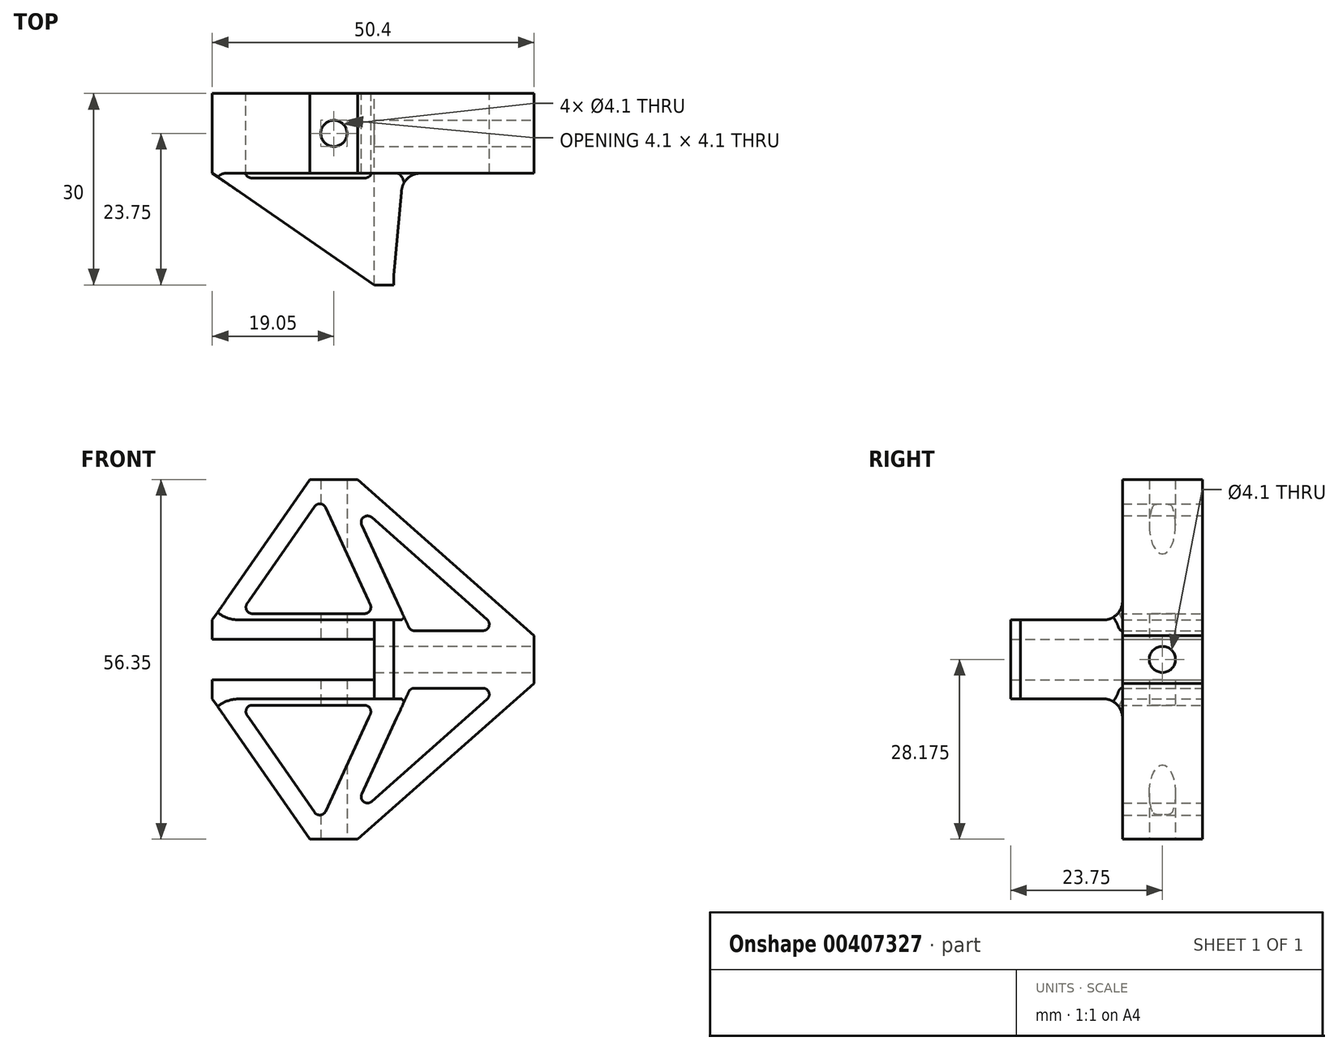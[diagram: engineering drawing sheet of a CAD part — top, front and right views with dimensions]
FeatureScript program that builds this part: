
annotation { "Feature Type Name" : "Feature", "Feature Type Description" : "" }
export const myFeature = defineFeature(function(context is Context, id is Id, definition is map)
    precondition{}
    {
        {
            var Q0;
            Q0=qCreatedBy(makeId("Front.planeOp"),FACE);
            var sketch = newSketch(context, id + "F0", { "sketchPlane" : qUnion([Q0])});
            skLineSegment(sketch, "E0", {"start": v(-37.84, 0) * mm, "end": v(0, 0) * mm, "construction": true});
            skLineSegment(sketch, "E1", {"start": v(0, 0) * mm, "end": v(0, -6.35) * mm, "construction": true});
            skLineSegment(sketch, "E2", {"start": v(0, -6.35) * mm, "end": v(-37.84, -6.35) * mm, "construction": true});
            skLineSegment(sketch, "E3", {"start": v(-12.7, -6.35) * mm, "end": v(-12.7, 0) * mm, "construction": true});
            skLineSegment(sketch, "E4", {"start": v(-4.3, -31.35) * mm, "end": v(-4.3, 20.4) * mm, "construction": true});
            skLineSegment(sketch, "E5", {"start": v(-4.3, 20.4) * mm, "end": v(-8.4, 20.4) * mm, "construction": true});
            skLineSegment(sketch, "E6", {"start": v(-8.4, 20.4) * mm, "end": v(-8.4, -31.35) * mm, "construction": true});
            skLineSegment(sketch, "E7", {"start": v(-8.4, -31.35) * mm, "end": v(-4.3, -31.35) * mm, "construction": true});
            skLineSegment(sketch, "E8", {"start": v(-6.35, -31.35) * mm, "end": v(-6.35, 20.4) * mm, "construction": true});
            skLineSegment(sketch, "E9", {"start": v(-25.4, -6.35) * mm, "end": v(-25.4, -9.35) * mm});
            skLineSegment(sketch, "E10", {"start": v(-25.4, -9.35) * mm, "end": v(-10.1, -31.35) * mm});
            skLineSegment(sketch, "E11", {"start": v(-10.1, -31.35) * mm, "end": v(-2.6, -31.35) * mm});
            skLineSegment(sketch, "E12", {"start": v(-2.6, -31.35) * mm, "end": v(25, -6.93) * mm});
            skLineSegment(sketch, "E13", {"start": v(25, -6.93) * mm, "end": v(25, -3.18) * mm});
            skLineSegment(sketch, "E14", {"start": v(0, -3.17) * mm, "end": v(-29.82, -3.17) * mm, "construction": true});
            skLineSegment(sketch, "E15", {"start": v(-25.4, -6.35) * mm, "end": v(0, -6.35) * mm});
            skLineSegment(sketch, "E16", {"start": v(0, -6.35) * mm, "end": v(0, -3.17) * mm});
            skLineSegment(sketch, "E17.MirrorCS", {"start": v(0, 0) * mm, "end": v(0, -3.17) * mm});
            skLineSegment(sketch, "E18.MirrorCS", {"start": v(-25.4, 0) * mm, "end": v(0, 0) * mm});
            skLineSegment(sketch, "E19.MirrorCS", {"start": v(-25.4, 0) * mm, "end": v(-25.4, 3) * mm});
            skLineSegment(sketch, "E20.MirrorCS", {"start": v(-25.4, 3) * mm, "end": v(-10.1, 25) * mm});
            skLineSegment(sketch, "E21.MirrorCS", {"start": v(-10.1, 25) * mm, "end": v(-2.6, 25) * mm});
            skLineSegment(sketch, "E22.MirrorCS", {"start": v(-2.6, 25) * mm, "end": v(25, 0.57) * mm});
            skLineSegment(sketch, "E23.MirrorCS", {"start": v(25, 0.57) * mm, "end": v(25, -3.18) * mm});
            skLineSegment(sketch, "E24", {"start": v(-19.96, -11.92) * mm, "end": v(-9.38, -27.13) * mm});
            skLineSegment(sketch, "E25", {"start": v(-7.65, -26.98) * mm, "end": v(-0.65, -11.77) * mm});
            skLineSegment(sketch, "E26", {"start": v(-1.56, -10.35) * mm, "end": v(-19.14, -10.35) * mm});
            skLineSegment(sketch, "E27", {"start": v(0, -3.17) * mm, "end": v(0, -28.47) * mm, "construction": true});
            skLineSegment(sketch, "E28", {"start": v(-0.42, -25.42) * mm, "end": v(17.65, -9.42) * mm});
            skLineSegment(sketch, "E29", {"start": v(16.99, -7.68) * mm, "end": v(6.27, -7.68) * mm});
            skLineSegment(sketch, "E30", {"start": v(5.37, -8.26) * mm, "end": v(-2, -24.25) * mm});
            skLineSegment(sketch, "E31", {"start": v(25, -5.22) * mm, "end": v(-10.9, -5.23) * mm, "construction": true});
            skLineSegment(sketch, "E32.MirrorCS", {"start": v(25, -1.13) * mm, "end": v(-10.9, -1.12) * mm, "construction": true});
            skLineSegment(sketch, "E33", {"start": v(-8.38, -28.56) * mm, "end": v(-3.98, -28.56) * mm, "construction": true});
            skPoint(sketch, "E34.visualSharp", {"position": v(-8.38, -28.56) * mm});
            skArc(sketch, "E34.filletArc", {"start": v(-9.38, -27.13) * mm, "mid": v(-8.47, -27.55) * mm, "end": v(-7.65, -26.98) * mm});
            skPoint(sketch, "E35.visualSharp", {"position": v(-3.98, -28.56) * mm});
            skArc(sketch, "E35.filletArc", {"start": v(-2, -24.25) * mm, "mid": v(-1.68, -25.47) * mm, "end": v(-0.42, -25.42) * mm});
            skPoint(sketch, "E36.visualSharp", {"position": v(19.63, -7.67) * mm});
            skArc(sketch, "E36.filletArc", {"start": v(17.65, -9.42) * mm, "mid": v(17.92, -8.32) * mm, "end": v(16.99, -7.68) * mm});
            skPoint(sketch, "E37.visualSharp", {"position": v(5.63, -7.67) * mm});
            skArc(sketch, "E37.filletArc", {"start": v(6.27, -7.67) * mm, "mid": v(5.74, -7.83) * mm, "end": v(5.37, -8.26) * mm});
            skPoint(sketch, "E38.visualSharp", {"position": v(0, -10.35) * mm});
            skArc(sketch, "E38.filletArc", {"start": v(-0.65, -11.77) * mm, "mid": v(-0.72, -10.81) * mm, "end": v(-1.56, -10.35) * mm});
            skPoint(sketch, "E39.visualSharp", {"position": v(-21.05, -10.35) * mm});
            skArc(sketch, "E39.filletArc", {"start": v(-19.14, -10.35) * mm, "mid": v(-20.02, -10.89) * mm, "end": v(-19.96, -11.92) * mm});
            skLineSegment(sketch, "E40.MirrorCS", {"start": v(-1.56, 4) * mm, "end": v(-19.14, 4) * mm});
            skArc(sketch, "E41.MirrorCS", {"start": v(-19.14, 4) * mm, "mid": v(-20.02, 4.54) * mm, "end": v(-19.96, 5.57) * mm});
            skLineSegment(sketch, "E42.MirrorCS", {"start": v(-19.96, 5.57) * mm, "end": v(-9.38, 20.78) * mm});
            skArc(sketch, "E43.MirrorCS", {"start": v(-9.38, 20.78) * mm, "mid": v(-8.47, 21.2) * mm, "end": v(-7.65, 20.63) * mm});
            skLineSegment(sketch, "E44.MirrorCS", {"start": v(-7.65, 20.63) * mm, "end": v(-0.65, 5.42) * mm});
            skArc(sketch, "E45.MirrorCS", {"start": v(-0.65, 5.42) * mm, "mid": v(-0.72, 4.46) * mm, "end": v(-1.56, 4) * mm});
            skLineSegment(sketch, "E46.MirrorCS", {"start": v(5.37, 1.9) * mm, "end": v(-2, 17.9) * mm});
            skArc(sketch, "E47.MirrorCS", {"start": v(-2, 17.9) * mm, "mid": v(-1.68, 19.12) * mm, "end": v(-0.42, 19.07) * mm});
            skLineSegment(sketch, "E48.MirrorCS", {"start": v(-0.42, 19.07) * mm, "end": v(17.65, 3.07) * mm});
            skArc(sketch, "E49.MirrorCS", {"start": v(17.65, 3.07) * mm, "mid": v(17.92, 1.97) * mm, "end": v(16.99, 1.33) * mm});
            skLineSegment(sketch, "E50.MirrorCS", {"start": v(16.99, 1.32) * mm, "end": v(6.27, 1.33) * mm});
            skArc(sketch, "E51.MirrorCS", {"start": v(6.27, 1.33) * mm, "mid": v(5.74, 1.48) * mm, "end": v(5.37, 1.9) * mm});
            skLineSegment(sketch, "E52", {"start": v(-25.4, -9.35) * mm, "end": v(3, -9.35) * mm});
            skLineSegment(sketch, "E53", {"start": v(-25.4, 3) * mm, "end": v(3, 3) * mm});
            skLineSegment(sketch, "E54", {"start": v(3, -9.35) * mm, "end": v(3, 3) * mm});
            skSolve(sketch);
        }
        {
            var Q0;
            Q0=makeQuery(id+"F0.imprint","IMPRINT",FACE,{"disambiguationData":[TD([[makeQuery(id+"F0.imprint","IMPRINT",EDGE,{"derivedFrom":sQuery(id+"F0.wireOp",EDGE,"E10")}),1.0]])]});
            var Q1;
            Q1=makeQuery(id+"F0.imprint","IMPRINT",FACE,{"disambiguationData":[TD([[makeQuery(id+"F0.imprint","IMPRINT",EDGE,{"derivedFrom":sQuery(id+"F0.wireOp",EDGE,"E9")}),1.0]])]});
            extrude(context, id + "F1", {"entities" : qUnion([Q0, Q1]), "depth" : 12.5 * mm});
        }
        {
            var Q0;
            Q0=makeQuery(id+"F0.imprint","IMPRINT",FACE,{"disambiguationData":[TD([[makeQuery(id+"F0.imprint","IMPRINT",EDGE,{"derivedFrom":sQuery(id+"F0.wireOp",EDGE,"E9")}),1.0]])]});
            extrude(context, id + "F2", {"entities" : qUnion([Q0]), "operationType" : NewBodyOperationType.ADD, "depth" : 30 * mm});
        }
        {
            var Q0;
            Q0=makeQuery(id+"F2.opExtrude","SWEPT_FACE",FACE,{"disambiguationData":[OSD([sQuery(id+"F0.wireOp",EDGE,"E53")])]});
            var sketch = newSketch(context, id + "F3", { "sketchPlane" : qUnion([Q0])});
            skLineSegment(sketch, "E55.1", {"start": v(3, -30) * mm, "end": v(3, -12.5) * mm});
            skLineSegment(sketch, "E55.2", {"start": v(3, -12.5) * mm, "end": v(-25.4, -12.5) * mm});
            skLineSegment(sketch, "E55.3", {"start": v(-25.4, -30) * mm, "end": v(-25.4, -12.5) * mm});
            skLineSegment(sketch, "E56.0", {"start": v(-25.4, -30) * mm, "end": v(0, -30) * mm});
            skLineSegment(sketch, "E57", {"start": v(0, -30) * mm, "end": v(-25.4, -12.5) * mm});
            skSolve(sketch);
        }
        {
            var Q0;
            Q0=makeQuery(id+"F3.imprint","IMPRINT",FACE,{"disambiguationData":[TD([[makeQuery(id+"F3.imprint","IMPRINT",EDGE,{"derivedFrom":sQuery(id+"F3.wireOp",EDGE,"E55.3")}),-1.0]])]});
            extrude(context, id + "F4", {"entities" : qUnion([Q0]), "operationType" : NewBodyOperationType.REMOVE, "endBound" : BoundingType.THROUGH_ALL, "oppositeDirection" : true, "depth" : 25 * mm});
        }
        {
            var Q0;
            Q0=makeQuery(id+"F1.opExtrude","SWEPT_FACE",FACE,{"disambiguationData":[OSD([sQuery(id+"F0.wireOp",EDGE,"E11")])]});
            var sketch = newSketch(context, id + "F5", { "sketchPlane" : qUnion([Q0])});
            skLineSegment(sketch, "E58", {"start": v(-6.35, 12.5) * mm, "end": v(-6.35, 0) * mm, "construction": true});
            skCircle(sketch, "E59", {"center": v(-6.35, 6.25) * mm, "radius": 2.05 * mm});
            skSolve(sketch);
        }
        {
            var Q0;
            Q0=makeQuery(id+"F5.imprint","IMPRINT",FACE,{"disambiguationData":[TD([[makeQuery(id+"F5.imprint","IMPRINT",EDGE,{"derivedFrom":sQuery(id+"F5.wireOp",EDGE,"E59")}),1.0]])]});
            extrude(context, id + "F6", {"entities" : qUnion([Q0]), "operationType" : NewBodyOperationType.REMOVE, "endBound" : BoundingType.THROUGH_ALL, "oppositeDirection" : true, "depth" : 25 * mm});
        }
        {
            var Q0;
            Q0=makeQuery(id+"F1.opExtrude","SWEPT_FACE",FACE,{"disambiguationData":[OSD([sQuery(id+"F0.wireOp",EDGE,"E13"),sQuery(id+"F0.wireOp",EDGE,"E23.MirrorCS")])]});
            var sketch = newSketch(context, id + "F7", { "sketchPlane" : qUnion([Q0])});
            skLineSegment(sketch, "E60", {"start": v(-12.5, -3.18) * mm, "end": v(0, -3.18) * mm, "construction": true});
            skCircle(sketch, "E61", {"center": v(-6.25, -3.18) * mm, "radius": 2.05 * mm});
            skSolve(sketch);
        }
        {
            var Q0;
            Q0=makeQuery(id+"F7.imprint","IMPRINT",FACE,{"disambiguationData":[TD([[makeQuery(id+"F7.imprint","IMPRINT",EDGE,{"derivedFrom":sQuery(id+"F7.wireOp",EDGE,"E61")}),1.0]])]});
            extrude(context, id + "F8", {"entities" : qUnion([Q0]), "operationType" : NewBodyOperationType.REMOVE, "endBound" : BoundingType.THROUGH_ALL, "oppositeDirection" : true, "depth" : 25 * mm});
        }
        {
            var Q0;
            Q0=makeQuery(id+"F2.boolean.opBoolean","INTERSECT",EDGE,{"derivedFrom":[makeQuery(id+"F1.opExtrude","CAP_FACE",FACE,{"disambiguationData":[OSD([sQuery(id+"F0.wireOp",EDGE,"E9"),sQuery(id+"F0.wireOp",EDGE,"E10"),sQuery(id+"F0.wireOp",EDGE,"E11"),sQuery(id+"F0.wireOp",EDGE,"E12"),sQuery(id+"F0.wireOp",EDGE,"E13"),sQuery(id+"F0.wireOp",EDGE,"E15"),sQuery(id+"F0.wireOp",EDGE,"E16"),sQuery(id+"F0.wireOp",EDGE,"E17.MirrorCS"),sQuery(id+"F0.wireOp",EDGE,"E18.MirrorCS"),sQuery(id+"F0.wireOp",EDGE,"E19.MirrorCS"),sQuery(id+"F0.wireOp",EDGE,"E20.MirrorCS"),sQuery(id+"F0.wireOp",EDGE,"E21.MirrorCS"),sQuery(id+"F0.wireOp",EDGE,"E22.MirrorCS"),sQuery(id+"F0.wireOp",EDGE,"E23.MirrorCS"),sQuery(id+"F0.wireOp",EDGE,"E24"),sQuery(id+"F0.wireOp",EDGE,"E25"),sQuery(id+"F0.wireOp",EDGE,"E26"),sQuery(id+"F0.wireOp",EDGE,"E28"),sQuery(id+"F0.wireOp",EDGE,"E29"),sQuery(id+"F0.wireOp",EDGE,"E30"),sQuery(id+"F0.wireOp",EDGE,"E34.filletArc"),sQuery(id+"F0.wireOp",EDGE,"E35.filletArc"),sQuery(id+"F0.wireOp",EDGE,"E36.filletArc"),sQuery(id+"F0.wireOp",EDGE,"E37.filletArc"),sQuery(id+"F0.wireOp",EDGE,"E38.filletArc"),sQuery(id+"F0.wireOp",EDGE,"E39.filletArc"),sQuery(id+"F0.wireOp",EDGE,"E40.MirrorCS"),sQuery(id+"F0.wireOp",EDGE,"E41.MirrorCS"),sQuery(id+"F0.wireOp",EDGE,"E42.MirrorCS"),sQuery(id+"F0.wireOp",EDGE,"E43.MirrorCS"),sQuery(id+"F0.wireOp",EDGE,"E44.MirrorCS"),sQuery(id+"F0.wireOp",EDGE,"E45.MirrorCS"),sQuery(id+"F0.wireOp",EDGE,"E46.MirrorCS"),sQuery(id+"F0.wireOp",EDGE,"E47.MirrorCS"),sQuery(id+"F0.wireOp",EDGE,"E48.MirrorCS"),sQuery(id+"F0.wireOp",EDGE,"E49.MirrorCS"),sQuery(id+"F0.wireOp",EDGE,"E50.MirrorCS"),sQuery(id+"F0.wireOp",EDGE,"E51.MirrorCS")])],"isStart":false}),makeQuery(id+"F2.opExtrude","SWEPT_FACE",FACE,{"disambiguationData":[OSD([sQuery(id+"F0.wireOp",EDGE,"E54")])]})]});
            chamfer(context, id + "F9", {"entities" : qUnion([Q0]), "chamferType" : ChamferType.TWO_OFFSETS, "width1" : 1.5 * mm, "oppositeDirection" : false, "width2" : 16 * mm, "tangentPropagation" : true});
        }
        {
            var Q0;
            Q0=makeQuery(id+"F2.boolean.opBoolean","INTERSECT",EDGE,{"derivedFrom":[makeQuery(id+"F1.opExtrude","CAP_FACE",FACE,{"disambiguationData":[OSD([sQuery(id+"F0.wireOp",EDGE,"E9"),sQuery(id+"F0.wireOp",EDGE,"E10"),sQuery(id+"F0.wireOp",EDGE,"E11"),sQuery(id+"F0.wireOp",EDGE,"E12"),sQuery(id+"F0.wireOp",EDGE,"E13"),sQuery(id+"F0.wireOp",EDGE,"E15"),sQuery(id+"F0.wireOp",EDGE,"E16"),sQuery(id+"F0.wireOp",EDGE,"E17.MirrorCS"),sQuery(id+"F0.wireOp",EDGE,"E18.MirrorCS"),sQuery(id+"F0.wireOp",EDGE,"E19.MirrorCS"),sQuery(id+"F0.wireOp",EDGE,"E20.MirrorCS"),sQuery(id+"F0.wireOp",EDGE,"E21.MirrorCS"),sQuery(id+"F0.wireOp",EDGE,"E22.MirrorCS"),sQuery(id+"F0.wireOp",EDGE,"E23.MirrorCS"),sQuery(id+"F0.wireOp",EDGE,"E24"),sQuery(id+"F0.wireOp",EDGE,"E25"),sQuery(id+"F0.wireOp",EDGE,"E26"),sQuery(id+"F0.wireOp",EDGE,"E28"),sQuery(id+"F0.wireOp",EDGE,"E29"),sQuery(id+"F0.wireOp",EDGE,"E30"),sQuery(id+"F0.wireOp",EDGE,"E34.filletArc"),sQuery(id+"F0.wireOp",EDGE,"E35.filletArc"),sQuery(id+"F0.wireOp",EDGE,"E36.filletArc"),sQuery(id+"F0.wireOp",EDGE,"E37.filletArc"),sQuery(id+"F0.wireOp",EDGE,"E38.filletArc"),sQuery(id+"F0.wireOp",EDGE,"E39.filletArc"),sQuery(id+"F0.wireOp",EDGE,"E40.MirrorCS"),sQuery(id+"F0.wireOp",EDGE,"E41.MirrorCS"),sQuery(id+"F0.wireOp",EDGE,"E42.MirrorCS"),sQuery(id+"F0.wireOp",EDGE,"E43.MirrorCS"),sQuery(id+"F0.wireOp",EDGE,"E44.MirrorCS"),sQuery(id+"F0.wireOp",EDGE,"E45.MirrorCS"),sQuery(id+"F0.wireOp",EDGE,"E46.MirrorCS"),sQuery(id+"F0.wireOp",EDGE,"E47.MirrorCS"),sQuery(id+"F0.wireOp",EDGE,"E48.MirrorCS"),sQuery(id+"F0.wireOp",EDGE,"E49.MirrorCS"),sQuery(id+"F0.wireOp",EDGE,"E50.MirrorCS"),sQuery(id+"F0.wireOp",EDGE,"E51.MirrorCS")])],"isStart":false}),makeQuery(id+"F2.opExtrude","SWEPT_FACE",FACE,{"disambiguationData":[OSD([sQuery(id+"F0.wireOp",EDGE,"E53")])]})]});
            var Q1;
            Q1=makeQuery(id+"F2.boolean.opBoolean","INTERSECT",EDGE,{"derivedFrom":[makeQuery(id+"F1.opExtrude","CAP_FACE",FACE,{"disambiguationData":[OSD([sQuery(id+"F0.wireOp",EDGE,"E9"),sQuery(id+"F0.wireOp",EDGE,"E10"),sQuery(id+"F0.wireOp",EDGE,"E11"),sQuery(id+"F0.wireOp",EDGE,"E12"),sQuery(id+"F0.wireOp",EDGE,"E13"),sQuery(id+"F0.wireOp",EDGE,"E15"),sQuery(id+"F0.wireOp",EDGE,"E16"),sQuery(id+"F0.wireOp",EDGE,"E17.MirrorCS"),sQuery(id+"F0.wireOp",EDGE,"E18.MirrorCS"),sQuery(id+"F0.wireOp",EDGE,"E19.MirrorCS"),sQuery(id+"F0.wireOp",EDGE,"E20.MirrorCS"),sQuery(id+"F0.wireOp",EDGE,"E21.MirrorCS"),sQuery(id+"F0.wireOp",EDGE,"E22.MirrorCS"),sQuery(id+"F0.wireOp",EDGE,"E23.MirrorCS"),sQuery(id+"F0.wireOp",EDGE,"E24"),sQuery(id+"F0.wireOp",EDGE,"E25"),sQuery(id+"F0.wireOp",EDGE,"E26"),sQuery(id+"F0.wireOp",EDGE,"E28"),sQuery(id+"F0.wireOp",EDGE,"E29"),sQuery(id+"F0.wireOp",EDGE,"E30"),sQuery(id+"F0.wireOp",EDGE,"E34.filletArc"),sQuery(id+"F0.wireOp",EDGE,"E35.filletArc"),sQuery(id+"F0.wireOp",EDGE,"E36.filletArc"),sQuery(id+"F0.wireOp",EDGE,"E37.filletArc"),sQuery(id+"F0.wireOp",EDGE,"E38.filletArc"),sQuery(id+"F0.wireOp",EDGE,"E39.filletArc"),sQuery(id+"F0.wireOp",EDGE,"E40.MirrorCS"),sQuery(id+"F0.wireOp",EDGE,"E41.MirrorCS"),sQuery(id+"F0.wireOp",EDGE,"E42.MirrorCS"),sQuery(id+"F0.wireOp",EDGE,"E43.MirrorCS"),sQuery(id+"F0.wireOp",EDGE,"E44.MirrorCS"),sQuery(id+"F0.wireOp",EDGE,"E45.MirrorCS"),sQuery(id+"F0.wireOp",EDGE,"E46.MirrorCS"),sQuery(id+"F0.wireOp",EDGE,"E47.MirrorCS"),sQuery(id+"F0.wireOp",EDGE,"E48.MirrorCS"),sQuery(id+"F0.wireOp",EDGE,"E49.MirrorCS"),sQuery(id+"F0.wireOp",EDGE,"E50.MirrorCS"),sQuery(id+"F0.wireOp",EDGE,"E51.MirrorCS")])],"isStart":false}),makeQuery(id+"F2.opExtrude","SWEPT_FACE",FACE,{"disambiguationData":[OSD([sQuery(id+"F0.wireOp",EDGE,"E52")])]})]});
            var Q2;
            {var subQ0=makeQuery(id+"F1.opExtrude","CAP_FACE",FACE,{"disambiguationData":[OSD([sQuery(id+"F0.wireOp",EDGE,"E9"),sQuery(id+"F0.wireOp",EDGE,"E10"),sQuery(id+"F0.wireOp",EDGE,"E11"),sQuery(id+"F0.wireOp",EDGE,"E12"),sQuery(id+"F0.wireOp",EDGE,"E13"),sQuery(id+"F0.wireOp",EDGE,"E15"),sQuery(id+"F0.wireOp",EDGE,"E16"),sQuery(id+"F0.wireOp",EDGE,"E17.MirrorCS"),sQuery(id+"F0.wireOp",EDGE,"E18.MirrorCS"),sQuery(id+"F0.wireOp",EDGE,"E19.MirrorCS"),sQuery(id+"F0.wireOp",EDGE,"E20.MirrorCS"),sQuery(id+"F0.wireOp",EDGE,"E21.MirrorCS"),sQuery(id+"F0.wireOp",EDGE,"E22.MirrorCS"),sQuery(id+"F0.wireOp",EDGE,"E23.MirrorCS"),sQuery(id+"F0.wireOp",EDGE,"E24"),sQuery(id+"F0.wireOp",EDGE,"E25"),sQuery(id+"F0.wireOp",EDGE,"E26"),sQuery(id+"F0.wireOp",EDGE,"E28"),sQuery(id+"F0.wireOp",EDGE,"E29"),sQuery(id+"F0.wireOp",EDGE,"E30"),sQuery(id+"F0.wireOp",EDGE,"E34.filletArc"),sQuery(id+"F0.wireOp",EDGE,"E35.filletArc"),sQuery(id+"F0.wireOp",EDGE,"E36.filletArc"),sQuery(id+"F0.wireOp",EDGE,"E37.filletArc"),sQuery(id+"F0.wireOp",EDGE,"E38.filletArc"),sQuery(id+"F0.wireOp",EDGE,"E39.filletArc"),sQuery(id+"F0.wireOp",EDGE,"E40.MirrorCS"),sQuery(id+"F0.wireOp",EDGE,"E41.MirrorCS"),sQuery(id+"F0.wireOp",EDGE,"E42.MirrorCS"),sQuery(id+"F0.wireOp",EDGE,"E43.MirrorCS"),sQuery(id+"F0.wireOp",EDGE,"E44.MirrorCS"),sQuery(id+"F0.wireOp",EDGE,"E45.MirrorCS"),sQuery(id+"F0.wireOp",EDGE,"E46.MirrorCS"),sQuery(id+"F0.wireOp",EDGE,"E47.MirrorCS"),sQuery(id+"F0.wireOp",EDGE,"E48.MirrorCS"),sQuery(id+"F0.wireOp",EDGE,"E49.MirrorCS"),sQuery(id+"F0.wireOp",EDGE,"E50.MirrorCS"),sQuery(id+"F0.wireOp",EDGE,"E51.MirrorCS")])],"isStart":false});Q2=makeQuery(id+"F9.opChamfer","BLEND_EDGE",EDGE,{"blendedFrom":[makeQuery(id+"F2.boolean.opBoolean","INTERSECT",EDGE,{"derivedFrom":[subQ0,makeQuery(id+"F2.opExtrude","SWEPT_FACE",FACE,{"disambiguationData":[OSD([sQuery(id+"F0.wireOp",EDGE,"E54")])]})]}),subQ0],"blendedInto":[subQ0]});}
            fillet(context, id + "F10", {"entities" : qUnion([Q0, Q1, Q2]), "radius" : 3 * mm, "tangentPropagation" : true, "allowEdgeOverflow" : false});
        }
    });
